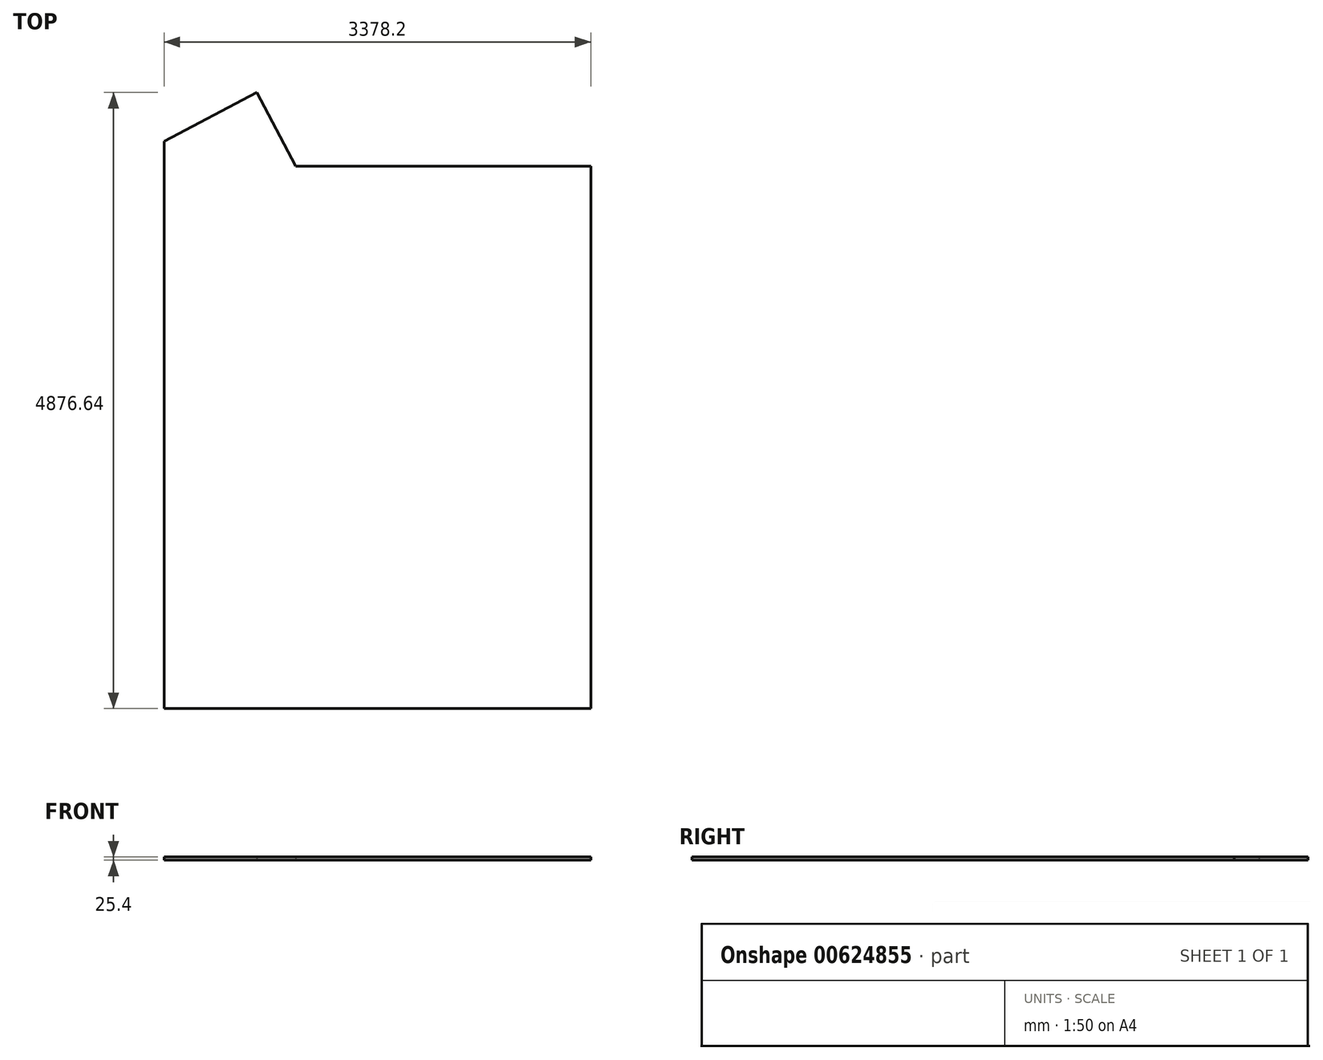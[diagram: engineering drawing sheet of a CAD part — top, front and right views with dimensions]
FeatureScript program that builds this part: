
annotation { "Feature Type Name" : "Feature", "Feature Type Description" : "" }
export const myFeature = defineFeature(function(context is Context, id is Id, definition is map)
    precondition{}
    {
        {
            var Q0;
            Q0=qCreatedBy(makeId("Top.planeOp"),FACE);
            var sketch = newSketch(context, id + "F0", { "sketchPlane" : qUnion([Q0])});
            skLineSegment(sketch, "E0", {"start": v(-2331.4, 1132.3) * mm, "end": v(-2331.4, -3357.41) * mm});
            skLineSegment(sketch, "E1", {"start": v(-2331.4, -3357.41) * mm, "end": v(1046.8, -3357.41) * mm});
            skLineSegment(sketch, "E2", {"start": v(1046.8, -3357.41) * mm, "end": v(1046.8, 935.19) * mm});
            skLineSegment(sketch, "E3", {"start": v(1046.8, 935.19) * mm, "end": v(-1290, 935.19) * mm});
            skLineSegment(sketch, "E4", {"start": v(-1290, 935.19) * mm, "end": v(-1598.25, 1519.23) * mm});
            skLineSegment(sketch, "E5", {"start": v(-1598.25, 1519.23) * mm, "end": v(-2331.4, 1132.3) * mm});
            skSolve(sketch);
        }
        {
            var Q0;
            Q0=makeQuery(id+"F0.imprint","IMPRINT",FACE,{"disambiguationData":[TD([[makeQuery(id+"F0.imprint","IMPRINT",EDGE,{"derivedFrom":sQuery(id+"F0.wireOp",EDGE,"E0")}),1.0]])]});
            extrude(context, id + "F1", {"entities" : qUnion([Q0]), "depth" : 25.4 * mm, "offsetDistance" : 25.4 * mm});
        }
    });
